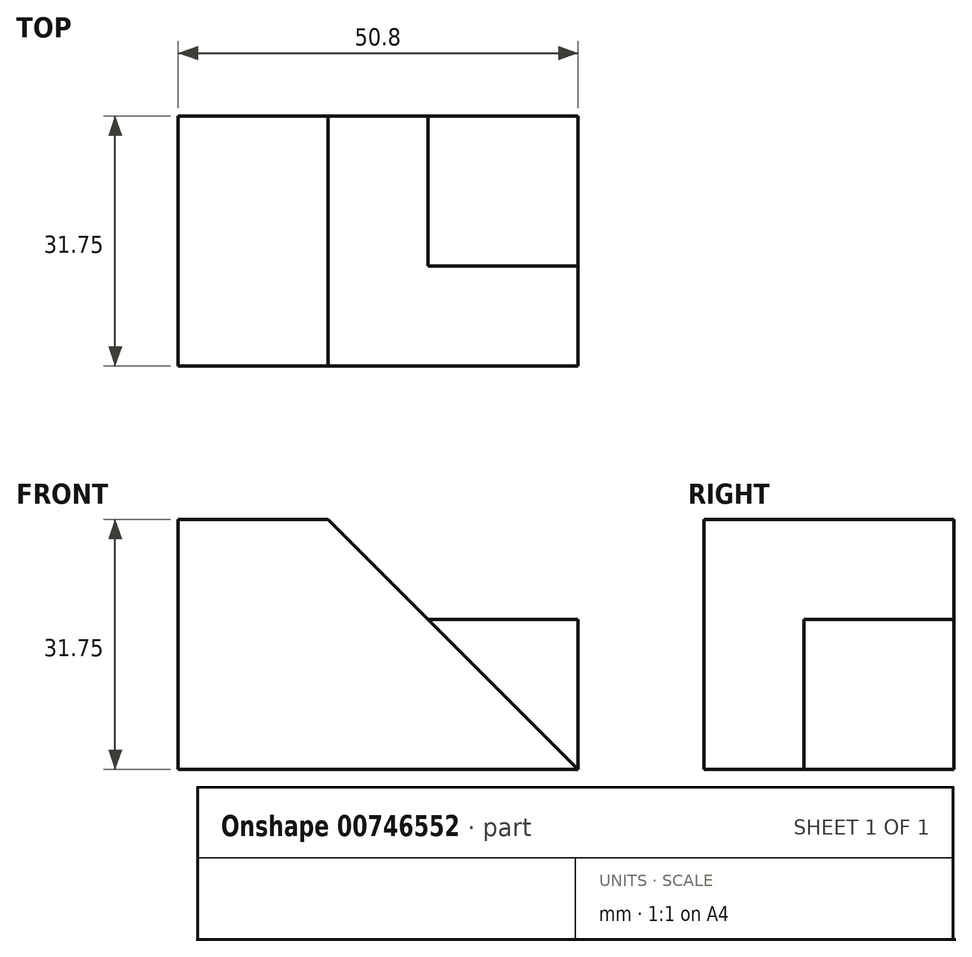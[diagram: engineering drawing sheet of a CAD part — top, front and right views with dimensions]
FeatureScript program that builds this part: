
annotation { "Feature Type Name" : "Feature", "Feature Type Description" : "" }
export const myFeature = defineFeature(function(context is Context, id is Id, definition is map)
    precondition{}
    {
        {
            var Q0;
            Q0=qCreatedBy(makeId("Front.planeOp"),FACE);
            var sketch = newSketch(context, id + "F0", { "sketchPlane" : qUnion([Q0])});
            skLineSegment(sketch, "E0.bottom", {"start": v(0, 0) * mm, "end": v(50.8, 0) * mm});
            skLineSegment(sketch, "E0.top", {"start": v(0, 31.75) * mm, "end": v(50.8, 31.75) * mm});
            skLineSegment(sketch, "E0.left", {"start": v(0, 0) * mm, "end": v(0, 31.75) * mm});
            skLineSegment(sketch, "E0.right", {"start": v(50.8, 0) * mm, "end": v(50.8, 31.75) * mm});
            skSolve(sketch);
        }
        {
            var Q0;
            Q0=makeQuery(id+"F0.imprint","IMPRINT",FACE,{"disambiguationData":[TD([[makeQuery(id+"F0.imprint","IMPRINT",EDGE,{"derivedFrom":sQuery(id+"F0.wireOp",EDGE,"E0.bottom")}),1.0]])]});
            extrude(context, id + "F1", {"entities" : qUnion([Q0]), "depth" : 31.75 * mm, "offsetDistance" : 25.4 * mm});
        }
        {
            var Q0;
            Q0=makeQuery(id+"F1.opExtrude","CAP_FACE",FACE,{"disambiguationData":[OSD([sQuery(id+"F0.wireOp",EDGE,"E0.bottom"),sQuery(id+"F0.wireOp",EDGE,"E0.top"),sQuery(id+"F0.wireOp",EDGE,"E0.left"),sQuery(id+"F0.wireOp",EDGE,"E0.right")])],"isStart":false});
            var sketch = newSketch(context, id + "F2", { "sketchPlane" : qUnion([Q0])});
            skLineSegment(sketch, "E1", {"start": v(19.05, 31.75) * mm, "end": v(50.8, 31.75) * mm});
            skLineSegment(sketch, "E2", {"start": v(19.05, 31.75) * mm, "end": v(50.8, 0) * mm});
            skLineSegment(sketch, "E3", {"start": v(50.8, 31.75) * mm, "end": v(50.8, 0) * mm});
            skSolve(sketch);
        }
        {
            var Q0;
            Q0=makeQuery(id+"F2.imprint","IMPRINT",FACE,{"disambiguationData":[TD([[makeQuery(id+"F2.imprint","IMPRINT",EDGE,{"derivedFrom":sQuery(id+"F2.wireOp",EDGE,"E1")}),-1.0]])]});
            extrude(context, id + "F3", {"entities" : qUnion([Q0]), "operationType" : NewBodyOperationType.REMOVE, "oppositeDirection" : true, "depth" : 31.75 * mm, "offsetDistance" : 25.4 * mm});
        }
        {
            var Q0;
            Q0=makeQuery(id+"F1.opExtrude","CAP_FACE",FACE,{"disambiguationData":[OSD([sQuery(id+"F0.wireOp",EDGE,"E0.bottom"),sQuery(id+"F0.wireOp",EDGE,"E0.top"),sQuery(id+"F0.wireOp",EDGE,"E0.left"),sQuery(id+"F0.wireOp",EDGE,"E0.right")])],"isStart":true});
            var sketch = newSketch(context, id + "F4", { "sketchPlane" : qUnion([Q0])});
            skLineSegment(sketch, "E4", {"start": v(-50.8, 0) * mm, "end": v(-31.75, 0) * mm});
            skLineSegment(sketch, "E5", {"start": v(-31.75, 0) * mm, "end": v(-31.75, 19.05) * mm});
            skLineSegment(sketch, "E6", {"start": v(-31.75, 19.05) * mm, "end": v(-50.8, 19.05) * mm});
            skLineSegment(sketch, "E7", {"start": v(-50.8, 19.05) * mm, "end": v(-50.8, 0) * mm});
            skSolve(sketch);
        }
        {
            var Q0;
            {var subQ0=sQuery(id+"F4.wireOp",EDGE,"E6");Q0=makeQuery(id+"F4.imprint","IMPRINT",FACE,{"disambiguationData":[TD([[makeQuery(id+"F4.imprint","IMPRINT",EDGE,{"derivedFrom":subQ0}),1.0]])]});}
            extrude(context, id + "F5", {"entities" : qUnion([Q0]), "operationType" : NewBodyOperationType.ADD, "oppositeDirection" : true, "depth" : 19.05 * mm, "offsetDistance" : 25.4 * mm});
        }
    });
